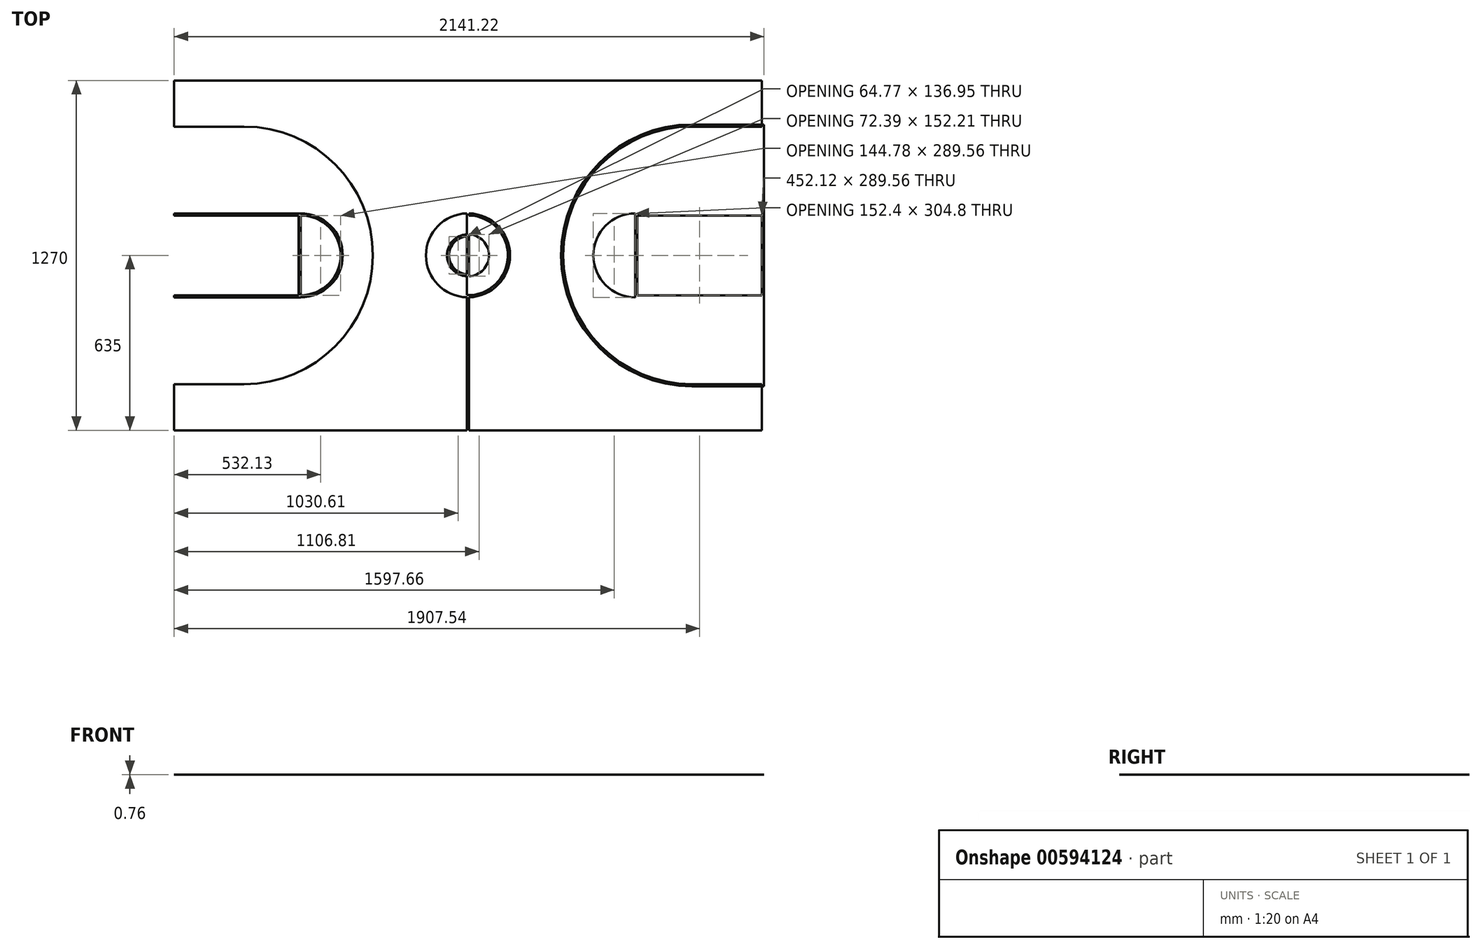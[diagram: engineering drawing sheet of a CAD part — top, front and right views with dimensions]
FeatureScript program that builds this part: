
annotation { "Feature Type Name" : "Feature", "Feature Type Description" : "" }
export const myFeature = defineFeature(function(context is Context, id is Id, definition is map)
    precondition{}
    {
        {
            var Q0;
            Q0=qCreatedBy(makeId("Top.planeOp"),FACE);
            var sketch = newSketch(context, id + "F0", { "sketchPlane" : qUnion([Q0])});
            skLineSegment(sketch, "E0.bottom", {"start": v(-1066.8, -635) * mm, "end": v(1066.8, -635) * mm});
            skLineSegment(sketch, "E0.top", {"start": v(-1066.8, 635) * mm, "end": v(1066.8, 635) * mm});
            skLineSegment(sketch, "E0.left", {"start": v(-1066.8, -635) * mm, "end": v(-1066.8, 635) * mm});
            skLineSegment(sketch, "E0.right", {"start": v(1066.8, -635) * mm, "end": v(1066.8, 635) * mm});
            skPoint(sketch, "E0.middle", {"position": v(0, 0) * mm});
            skLineSegment(sketch, "E1.bottom", {"start": v(-3.81, -635) * mm, "end": v(3.81, -635) * mm});
            skLineSegment(sketch, "E1.top", {"start": v(-3.81, 635) * mm, "end": v(3.81, 635) * mm});
            skLineSegment(sketch, "E1.left", {"start": v(-3.81, -635) * mm, "end": v(-3.81, 635) * mm});
            skLineSegment(sketch, "E1.right", {"start": v(3.81, -635) * mm, "end": v(3.81, 635) * mm});
            skCircle(sketch, "E2", {"center": v(0, 0) * mm, "radius": 152.4 * mm});
            skCircle(sketch, "E3", {"center": v(0, 0) * mm, "radius": 144.78 * mm});
            skCircle(sketch, "E4", {"center": v(0, 0) * mm, "radius": 76.2 * mm});
            skCircle(sketch, "E5", {"center": v(0, 0) * mm, "radius": 68.58 * mm});
            skPoint(sketch, "E6.endSnap0", {"position": v(-1066.8, 0) * mm});
            skLineSegment(sketch, "E7.bottom", {"start": v(-1066.8, -152.4) * mm, "end": v(-607.06, -152.4) * mm});
            skLineSegment(sketch, "E7.top", {"start": v(-1066.8, 152.4) * mm, "end": v(-607.06, 152.4) * mm});
            skLineSegment(sketch, "E7.left", {"start": v(-1066.8, -152.4) * mm, "end": v(-1066.8, 152.4) * mm});
            skLineSegment(sketch, "E7.right", {"start": v(-607.06, -152.4) * mm, "end": v(-607.06, 152.4) * mm});
            skPoint(sketch, "E7.middle", {"position": v(-836.93, 0) * mm});
            skPoint(sketch, "E6.end.orphan", {"position": v(-607.06, 0) * mm});
            skArc(sketch, "E8", {"start": v(-607.06, -152.4) * mm, "mid": v(-454.66, 0) * mm, "end": v(-607.06, 152.4) * mm});
            skLineSegment(sketch, "E9", {"start": v(-1066.8, 635) * mm, "end": v(-1066.8, 474.98) * mm});
            skLineSegment(sketch, "E10", {"start": v(-1066.8, -635) * mm, "end": v(-1066.8, -474.98) * mm});
            skLineSegment(sketch, "E11", {"start": v(-1066.8, 474.98) * mm, "end": v(-812.8, 474.98) * mm});
            skLineSegment(sketch, "E12", {"start": v(-1066.8, -474.98) * mm, "end": v(-812.8, -474.98) * mm});
            skArc(sketch, "E13", {"start": v(-812.8, -474.98) * mm, "mid": v(-337.82, 0) * mm, "end": v(-812.8, 474.98) * mm});
            skLineSegment(sketch, "E14", {"start": v(0, 635) * mm, "end": v(0, -635) * mm});
            skArc(sketch, "E15.MirrorCS", {"start": v(812.8, -474.98) * mm, "mid": v(337.82, 0) * mm, "end": v(812.8, 474.98) * mm});
            skArc(sketch, "E16.MirrorCS", {"start": v(607.06, -152.4) * mm, "mid": v(454.66, 0) * mm, "end": v(607.06, 152.4) * mm});
            skLineSegment(sketch, "E17.MirrorCS", {"start": v(607.06, -152.4) * mm, "end": v(607.06, 152.4) * mm});
            skLineSegment(sketch, "E18.MirrorCS", {"start": v(1066.8, -474.98) * mm, "end": v(812.8, -474.98) * mm});
            skLineSegment(sketch, "E19.MirrorCS", {"start": v(1066.8, 474.98) * mm, "end": v(812.8, 474.98) * mm});
            skLineSegment(sketch, "E20.MirrorCS", {"start": v(1066.8, 152.4) * mm, "end": v(607.06, 152.4) * mm});
            skLineSegment(sketch, "E21.MirrorCS", {"start": v(1066.8, -152.4) * mm, "end": v(607.06, -152.4) * mm});
            skLineSegment(sketch, "E22", {"start": v(-1066.8, 474.98) * mm, "end": v(-1066.8, 467.36) * mm});
            skLineSegment(sketch, "E23", {"start": v(-1066.8, 467.36) * mm, "end": v(-812.8, 467.36) * mm});
            skLineSegment(sketch, "E24", {"start": v(-812.8, 467.36) * mm, "end": v(-812.8, 474.98) * mm});
            skLineSegment(sketch, "E25", {"start": v(-1066.8, -474.98) * mm, "end": v(-1066.8, -467.36) * mm});
            skLineSegment(sketch, "E26", {"start": v(-1066.8, -467.36) * mm, "end": v(-812.8, -467.36) * mm});
            skArc(sketch, "E27", {"start": v(-812.8, -467.36) * mm, "mid": v(-345.44, 0) * mm, "end": v(-812.8, 467.36) * mm});
            skLineSegment(sketch, "E28", {"start": v(-1066.8, 152.4) * mm, "end": v(-1066.8, 144.78) * mm});
            skLineSegment(sketch, "E29", {"start": v(-1066.8, 144.78) * mm, "end": v(-607.06, 144.78) * mm});
            skLineSegment(sketch, "E30", {"start": v(-1066.8, -152.4) * mm, "end": v(-1066.8, -144.78) * mm});
            skLineSegment(sketch, "E31", {"start": v(-1066.8, -144.78) * mm, "end": v(-607.06, -144.78) * mm});
            skLineSegment(sketch, "E32", {"start": v(-607.06, 152.4) * mm, "end": v(-614.68, 152.4) * mm});
            skLineSegment(sketch, "E33", {"start": v(-614.68, 152.4) * mm, "end": v(-614.68, -152.4) * mm});
            skLineSegment(sketch, "E34", {"start": v(-614.68, -152.4) * mm, "end": v(-607.06, -152.4) * mm});
            skArc(sketch, "E35", {"start": v(-607.06, -144.78) * mm, "mid": v(-462.28, 0) * mm, "end": v(-607.06, 144.78) * mm});
            skArc(sketch, "E36.MirrorCS", {"start": v(812.8, -467.36) * mm, "mid": v(345.44, 0) * mm, "end": v(812.8, 467.36) * mm});
            skArc(sketch, "E37.MirrorCS", {"start": v(607.06, -144.78) * mm, "mid": v(462.28, 0) * mm, "end": v(607.06, 144.78) * mm});
            skLineSegment(sketch, "E38.MirrorCS", {"start": v(614.68, 152.4) * mm, "end": v(614.68, -152.4) * mm});
            skLineSegment(sketch, "E39.MirrorCS", {"start": v(1066.8, -144.78) * mm, "end": v(607.06, -144.78) * mm});
            skLineSegment(sketch, "E40.MirrorCS", {"start": v(1066.8, 144.78) * mm, "end": v(607.06, 144.78) * mm});
            skLineSegment(sketch, "E41.MirrorCS", {"start": v(1066.8, -467.36) * mm, "end": v(812.8, -467.36) * mm});
            skLineSegment(sketch, "E42.MirrorCS", {"start": v(1066.8, 467.36) * mm, "end": v(812.8, 467.36) * mm});
            skLineSegment(sketch, "E43", {"start": v(1066.8, 474.98) * mm, "end": v(1074.42, 474.98) * mm});
            skLineSegment(sketch, "E44", {"start": v(1074.42, 474.98) * mm, "end": v(1074.42, -474.98) * mm});
            skLineSegment(sketch, "E45", {"start": v(1074.42, -474.98) * mm, "end": v(1066.8, -474.98) * mm});
            skLineSegment(sketch, "E46.MirrorCS", {"start": v(-1074.42, -474.98) * mm, "end": v(-1066.8, -474.98) * mm});
            skLineSegment(sketch, "E47.MirrorCS", {"start": v(-1074.42, 474.98) * mm, "end": v(-1074.42, -474.98) * mm});
            skLineSegment(sketch, "E48.MirrorCS", {"start": v(-1066.8, 474.98) * mm, "end": v(-1074.42, 474.98) * mm});
            skSolve(sketch);
        }
        {
            var Q0;
            Q0=makeQuery(id+"F0.imprint","IMPRINT",FACE,{"disambiguationData":[TD([[makeQuery(id+"F0.imprint","IMPRINT",EDGE,{"derivedFrom":sQuery(id+"F0.wireOp",EDGE,"E12")}),1.0]])]});
            var Q1;
            Q1=makeQuery(id+"F0.imprint","IMPRINT",FACE,{"disambiguationData":[TD([[makeQuery(id+"F0.imprint","IMPRINT",EDGE,{"derivedFrom":sQuery(id+"F0.wireOp",EDGE,"E11")}),-1.0]])]});
            var Q2;
            {var subQ1=sQuery(id+"F0.wireOp",EDGE,"E29");var subQ6=sQuery(id+"F0.wireOp",EDGE,"E33");var subQ7=makeQuery(id+"F0.imprint","INTERSECT",VERTEX,{"derivedFrom":[subQ1,subQ6]});Q2=makeQuery(id+"F0.imprint","IMPRINT",FACE,{"disambiguationData":[TD([[makeQuery(id+"F0.imprint","IMPRINT",EDGE,{"disambiguationData":[TD([[subQ7,-1.0]])],"derivedFrom":subQ6}),1.0]])]});}
            var Q3;
            {var subQ0=sQuery(id+"F0.wireOp",EDGE,"E7.top");Q3=makeQuery(id+"F0.imprint","IMPRINT",FACE,{"disambiguationData":[TD([[makeQuery(id+"F0.imprint","IMPRINT",EDGE,{"derivedFrom":subQ0}),-1.0]])]});}
            var Q4;
            {var subQ0=sQuery(id+"F0.wireOp",EDGE,"E32");Q4=makeQuery(id+"F0.imprint","IMPRINT",FACE,{"disambiguationData":[TD([[makeQuery(id+"F0.imprint","IMPRINT",EDGE,{"derivedFrom":subQ0}),1.0]])]});}
            var Q5;
            {var subQ0=sQuery(id+"F0.wireOp",EDGE,"E8");Q5=makeQuery(id+"F0.imprint","IMPRINT",FACE,{"disambiguationData":[TD([[makeQuery(id+"F0.imprint","IMPRINT",EDGE,{"derivedFrom":subQ0}),1.0]])]});}
            var Q6;
            {var subQ0=sQuery(id+"F0.wireOp",EDGE,"E7.bottom");Q6=makeQuery(id+"F0.imprint","IMPRINT",FACE,{"disambiguationData":[TD([[makeQuery(id+"F0.imprint","IMPRINT",EDGE,{"derivedFrom":subQ0}),1.0]])]});}
            var Q7;
            {var subQ0=sQuery(id+"F0.wireOp",EDGE,"E34");Q7=makeQuery(id+"F0.imprint","IMPRINT",FACE,{"disambiguationData":[TD([[makeQuery(id+"F0.imprint","IMPRINT",EDGE,{"derivedFrom":subQ0}),1.0]])]});}
            var Q8;
            {var subQ0=sQuery(id+"F0.wireOp",EDGE,"E4");var subQ1=sQuery(id+"F0.wireOp",EDGE,"E1.left");var subQ2=makeQuery(id+"F0.imprint","INTERSECT",VERTEX,{"disambiguationData":[OD(0.0)],"derivedFrom":[subQ1,subQ0]});Q8=makeQuery(id+"F0.imprint","IMPRINT",FACE,{"disambiguationData":[TD([[makeQuery(id+"F0.imprint","IMPRINT",EDGE,{"disambiguationData":[TD([[subQ2,-1.0]])],"derivedFrom":subQ1}),1.0]])]});}
            var Q9;
            {var subQ0=sQuery(id+"F0.wireOp",EDGE,"E4");var subQ1=sQuery(id+"F0.wireOp",EDGE,"E1.right");var subQ2=makeQuery(id+"F0.imprint","INTERSECT",VERTEX,{"disambiguationData":[OD(0.0)],"derivedFrom":[subQ1,subQ0]});Q9=makeQuery(id+"F0.imprint","IMPRINT",FACE,{"disambiguationData":[TD([[makeQuery(id+"F0.imprint","IMPRINT",EDGE,{"disambiguationData":[TD([[subQ2,-1.0]])],"derivedFrom":subQ1}),-1.0]])]});}
            var Q10;
            {var subQ0=sQuery(id+"F0.wireOp",EDGE,"E5");var subQ1=sQuery(id+"F0.wireOp",EDGE,"E1.right");var subQ2=makeQuery(id+"F0.imprint","INTERSECT",VERTEX,{"disambiguationData":[OD(1.0)],"derivedFrom":[subQ1,subQ0]});Q10=makeQuery(id+"F0.imprint","IMPRINT",FACE,{"disambiguationData":[TD([[makeQuery(id+"F0.imprint","IMPRINT",EDGE,{"disambiguationData":[TD([[subQ2,-1.0]])],"derivedFrom":subQ1}),1.0]])]});}
            var Q11;
            {var subQ0=sQuery(id+"F0.wireOp",EDGE,"E5");var subQ1=sQuery(id+"F0.wireOp",EDGE,"E1.left");var subQ2=makeQuery(id+"F0.imprint","INTERSECT",VERTEX,{"disambiguationData":[OD(1.0)],"derivedFrom":[subQ1,subQ0]});Q11=makeQuery(id+"F0.imprint","IMPRINT",FACE,{"disambiguationData":[TD([[makeQuery(id+"F0.imprint","IMPRINT",EDGE,{"disambiguationData":[TD([[subQ2,-1.0]])],"derivedFrom":subQ1}),-1.0]])]});}
            var Q12;
            {var subQ0=sQuery(id+"F0.wireOp",EDGE,"E2");var subQ1=sQuery(id+"F0.wireOp",EDGE,"E1.left");var subQ2=makeQuery(id+"F0.imprint","INTERSECT",VERTEX,{"disambiguationData":[OD(0.0)],"derivedFrom":[subQ1,subQ0]});Q12=makeQuery(id+"F0.imprint","IMPRINT",FACE,{"disambiguationData":[TD([[makeQuery(id+"F0.imprint","IMPRINT",EDGE,{"disambiguationData":[TD([[subQ2,-1.0]])],"derivedFrom":subQ1}),1.0]])]});}
            var Q13;
            {var subQ0=sQuery(id+"F0.wireOp",EDGE,"E3");var subQ1=sQuery(id+"F0.wireOp",EDGE,"E1.left");var subQ2=makeQuery(id+"F0.imprint","INTERSECT",VERTEX,{"disambiguationData":[OD(1.0)],"derivedFrom":[subQ1,subQ0]});Q13=makeQuery(id+"F0.imprint","IMPRINT",FACE,{"disambiguationData":[TD([[makeQuery(id+"F0.imprint","IMPRINT",EDGE,{"disambiguationData":[TD([[subQ2,-1.0]])],"derivedFrom":subQ1}),-1.0]])]});}
            var Q14;
            {var subQ0=sQuery(id+"F0.wireOp",EDGE,"E3");var subQ1=sQuery(id+"F0.wireOp",EDGE,"E1.right");var subQ2=makeQuery(id+"F0.imprint","INTERSECT",VERTEX,{"disambiguationData":[OD(1.0)],"derivedFrom":[subQ1,subQ0]});Q14=makeQuery(id+"F0.imprint","IMPRINT",FACE,{"disambiguationData":[TD([[makeQuery(id+"F0.imprint","IMPRINT",EDGE,{"disambiguationData":[TD([[subQ2,-1.0]])],"derivedFrom":subQ1}),1.0]])]});}
            var Q15;
            {var subQ0=sQuery(id+"F0.wireOp",EDGE,"E2");var subQ1=sQuery(id+"F0.wireOp",EDGE,"E1.right");var subQ2=makeQuery(id+"F0.imprint","INTERSECT",VERTEX,{"disambiguationData":[OD(0.0)],"derivedFrom":[subQ1,subQ0]});Q15=makeQuery(id+"F0.imprint","IMPRINT",FACE,{"disambiguationData":[TD([[makeQuery(id+"F0.imprint","IMPRINT",EDGE,{"disambiguationData":[TD([[subQ2,-1.0]])],"derivedFrom":subQ1}),-1.0]])]});}
            var Q16;
            {var subQ0=sQuery(id+"F0.wireOp",EDGE,"E4");var subQ1=sQuery(id+"F0.wireOp",EDGE,"E1.left");var subQ2=makeQuery(id+"F0.imprint","INTERSECT",VERTEX,{"disambiguationData":[OD(0.0)],"derivedFrom":[subQ1,subQ0]});Q16=makeQuery(id+"F0.imprint","IMPRINT",FACE,{"disambiguationData":[TD([[makeQuery(id+"F0.imprint","IMPRINT",EDGE,{"disambiguationData":[TD([[subQ2,-1.0]])],"derivedFrom":subQ1}),-1.0]])]});}
            var Q17;
            {var subQ0=sQuery(id+"F0.wireOp",EDGE,"E4");var subQ1=sQuery(id+"F0.wireOp",EDGE,"E1.right");var subQ2=makeQuery(id+"F0.imprint","INTERSECT",VERTEX,{"disambiguationData":[OD(0.0)],"derivedFrom":[subQ1,subQ0]});Q17=makeQuery(id+"F0.imprint","IMPRINT",FACE,{"disambiguationData":[TD([[makeQuery(id+"F0.imprint","IMPRINT",EDGE,{"disambiguationData":[TD([[subQ2,-1.0]])],"derivedFrom":subQ1}),1.0]])]});}
            var Q18;
            {var subQ0=sQuery(id+"F0.wireOp",EDGE,"E2");var subQ1=sQuery(id+"F0.wireOp",EDGE,"E1.left");var subQ2=makeQuery(id+"F0.imprint","INTERSECT",VERTEX,{"disambiguationData":[OD(0.0)],"derivedFrom":[subQ1,subQ0]});Q18=makeQuery(id+"F0.imprint","IMPRINT",FACE,{"disambiguationData":[TD([[makeQuery(id+"F0.imprint","IMPRINT",EDGE,{"disambiguationData":[TD([[subQ2,-1.0]])],"derivedFrom":subQ1}),-1.0]])]});}
            var Q19;
            {var subQ0=sQuery(id+"F0.wireOp",EDGE,"E2");var subQ1=sQuery(id+"F0.wireOp",EDGE,"E1.right");var subQ2=makeQuery(id+"F0.imprint","INTERSECT",VERTEX,{"disambiguationData":[OD(0.0)],"derivedFrom":[subQ1,subQ0]});Q19=makeQuery(id+"F0.imprint","IMPRINT",FACE,{"disambiguationData":[TD([[makeQuery(id+"F0.imprint","IMPRINT",EDGE,{"disambiguationData":[TD([[subQ2,-1.0]])],"derivedFrom":subQ1}),1.0]])]});}
            var Q20;
            Q20=makeQuery(id+"F0.imprint","IMPRINT",FACE,{"disambiguationData":[TD([[makeQuery(id+"F0.imprint","IMPRINT",EDGE,{"derivedFrom":sQuery(id+"F0.wireOp",EDGE,"E15.MirrorCS")}),-1.0]])]});
            var Q21;
            {var subQ0=sQuery(id+"F0.wireOp",EDGE,"E20.MirrorCS");var subQ1=sQuery(id+"F0.wireOp",EDGE,"E0.right");var subQ2=makeQuery(id+"F0.imprint","INTERSECT",VERTEX,{"derivedFrom":[subQ1,subQ0]});Q21=makeQuery(id+"F0.imprint","IMPRINT",FACE,{"disambiguationData":[TD([[makeQuery(id+"F0.imprint","IMPRINT",EDGE,{"disambiguationData":[TD([[subQ2,1.0]])],"derivedFrom":subQ1}),1.0]])]});}
            var Q22;
            {var subQ0=sQuery(id+"F0.wireOp",EDGE,"E20.MirrorCS");var subQ5=sQuery(id+"F0.wireOp",EDGE,"E38.MirrorCS");var subQ6=makeQuery(id+"F0.imprint","INTERSECT",VERTEX,{"derivedFrom":[subQ0,subQ5]});Q22=makeQuery(id+"F0.imprint","IMPRINT",FACE,{"disambiguationData":[TD([[makeQuery(id+"F0.imprint","IMPRINT",EDGE,{"disambiguationData":[TD([[subQ6,-1.0]])],"derivedFrom":subQ5}),-1.0]])]});}
            var Q23;
            {var subQ4=sQuery(id+"F0.wireOp",EDGE,"E40.MirrorCS");var subQ6=sQuery(id+"F0.wireOp",EDGE,"E38.MirrorCS");var subQ7=makeQuery(id+"F0.imprint","INTERSECT",VERTEX,{"derivedFrom":[subQ6,subQ4]});Q23=makeQuery(id+"F0.imprint","IMPRINT",FACE,{"disambiguationData":[TD([[makeQuery(id+"F0.imprint","IMPRINT",EDGE,{"disambiguationData":[TD([[subQ7,-1.0]])],"derivedFrom":subQ6}),-1.0]])]});}
            var Q24;
            {var subQ0=sQuery(id+"F0.wireOp",EDGE,"E16.MirrorCS");Q24=makeQuery(id+"F0.imprint","IMPRINT",FACE,{"disambiguationData":[TD([[makeQuery(id+"F0.imprint","IMPRINT",EDGE,{"derivedFrom":subQ0}),-1.0]])]});}
            var Q25;
            {var subQ0=sQuery(id+"F0.wireOp",EDGE,"E21.MirrorCS");var subQ1=sQuery(id+"F0.wireOp",EDGE,"E0.right");var subQ2=makeQuery(id+"F0.imprint","INTERSECT",VERTEX,{"derivedFrom":[subQ1,subQ0]});Q25=makeQuery(id+"F0.imprint","IMPRINT",FACE,{"disambiguationData":[TD([[makeQuery(id+"F0.imprint","IMPRINT",EDGE,{"disambiguationData":[TD([[subQ2,-1.0]])],"derivedFrom":subQ1}),1.0]])]});}
            var Q26;
            {var subQ0=sQuery(id+"F0.wireOp",EDGE,"E21.MirrorCS");var subQ5=sQuery(id+"F0.wireOp",EDGE,"E38.MirrorCS");var subQ6=makeQuery(id+"F0.imprint","INTERSECT",VERTEX,{"derivedFrom":[subQ0,subQ5]});Q26=makeQuery(id+"F0.imprint","IMPRINT",FACE,{"disambiguationData":[TD([[makeQuery(id+"F0.imprint","IMPRINT",EDGE,{"disambiguationData":[TD([[subQ6,1.0]])],"derivedFrom":subQ5}),-1.0]])]});}
            var Q27;
            {var subQ8=sQuery(id+"F0.wireOp",EDGE,"E43");Q27=makeQuery(id+"F0.imprint","IMPRINT",FACE,{"disambiguationData":[TD([[makeQuery(id+"F0.imprint","IMPRINT",EDGE,{"derivedFrom":subQ8}),-1.0]])]});}
            var Q28;
            Q28=makeQuery(id+"F0.imprint","IMPRINT",FACE,{"disambiguationData":[TD([[makeQuery(id+"F0.imprint","IMPRINT",EDGE,{"derivedFrom":sQuery(id+"F0.wireOp",EDGE,"E7.left")}),1.0]])]});
            var Q29;
            {var subQ0=sQuery(id+"F0.wireOp",EDGE,"E1.left");var subQ5=sQuery(id+"F0.wireOp",EDGE,"E2");var subQ6=makeQuery(id+"F0.imprint","INTERSECT",VERTEX,{"disambiguationData":[OD(1.0)],"derivedFrom":[subQ0,subQ5]});Q29=makeQuery(id+"F0.imprint","IMPRINT",FACE,{"disambiguationData":[TD([[makeQuery(id+"F0.imprint","IMPRINT",EDGE,{"disambiguationData":[TD([[subQ6,1.0]])],"derivedFrom":subQ5}),-1.0]])]});}
            var Q30;
            {var subQ0=sQuery(id+"F0.wireOp",EDGE,"E1.right");var subQ5=sQuery(id+"F0.wireOp",EDGE,"E2");var subQ7=makeQuery(id+"F0.imprint","INTERSECT",VERTEX,{"disambiguationData":[OD(1.0)],"derivedFrom":[subQ0,subQ5]});Q30=makeQuery(id+"F0.imprint","IMPRINT",FACE,{"disambiguationData":[TD([[makeQuery(id+"F0.imprint","IMPRINT",EDGE,{"disambiguationData":[TD([[subQ7,-1.0]])],"derivedFrom":subQ5}),-1.0]])]});}
            var Q31;
            {var subQ0=sQuery(id+"F0.wireOp",EDGE,"E4");var subQ1=sQuery(id+"F0.wireOp",EDGE,"E1.left");var subQ2=makeQuery(id+"F0.imprint","INTERSECT",VERTEX,{"disambiguationData":[OD(1.0)],"derivedFrom":[subQ1,subQ0]});Q31=makeQuery(id+"F0.imprint","IMPRINT",FACE,{"disambiguationData":[TD([[makeQuery(id+"F0.imprint","IMPRINT",EDGE,{"disambiguationData":[TD([[subQ2,-1.0]])],"derivedFrom":subQ1}),-1.0]])]});}
            var Q32;
            {var subQ0=sQuery(id+"F0.wireOp",EDGE,"E4");var subQ1=sQuery(id+"F0.wireOp",EDGE,"E1.right");var subQ2=makeQuery(id+"F0.imprint","INTERSECT",VERTEX,{"disambiguationData":[OD(1.0)],"derivedFrom":[subQ1,subQ0]});Q32=makeQuery(id+"F0.imprint","IMPRINT",FACE,{"disambiguationData":[TD([[makeQuery(id+"F0.imprint","IMPRINT",EDGE,{"disambiguationData":[TD([[subQ2,-1.0]])],"derivedFrom":subQ1}),1.0]])]});}
            var Q33;
            {var subQ0=sQuery(id+"F0.wireOp",EDGE,"E5");var subQ1=sQuery(id+"F0.wireOp",EDGE,"E1.left");var subQ2=makeQuery(id+"F0.imprint","INTERSECT",VERTEX,{"disambiguationData":[OD(0.0)],"derivedFrom":[subQ1,subQ0]});Q33=makeQuery(id+"F0.imprint","IMPRINT",FACE,{"disambiguationData":[TD([[makeQuery(id+"F0.imprint","IMPRINT",EDGE,{"disambiguationData":[TD([[subQ2,-1.0]])],"derivedFrom":subQ1}),-1.0]])]});}
            var Q34;
            {var subQ0=sQuery(id+"F0.wireOp",EDGE,"E5");var subQ1=sQuery(id+"F0.wireOp",EDGE,"E1.right");var subQ2=makeQuery(id+"F0.imprint","INTERSECT",VERTEX,{"disambiguationData":[OD(0.0)],"derivedFrom":[subQ1,subQ0]});Q34=makeQuery(id+"F0.imprint","IMPRINT",FACE,{"disambiguationData":[TD([[makeQuery(id+"F0.imprint","IMPRINT",EDGE,{"disambiguationData":[TD([[subQ2,-1.0]])],"derivedFrom":subQ1}),1.0]])]});}
            var Q35;
            {var subQ0=sQuery(id+"F0.wireOp",EDGE,"E3");var subQ1=sQuery(id+"F0.wireOp",EDGE,"E1.left");var subQ2=makeQuery(id+"F0.imprint","INTERSECT",VERTEX,{"disambiguationData":[OD(0.0)],"derivedFrom":[subQ1,subQ0]});Q35=makeQuery(id+"F0.imprint","IMPRINT",FACE,{"disambiguationData":[TD([[makeQuery(id+"F0.imprint","IMPRINT",EDGE,{"disambiguationData":[TD([[subQ2,-1.0]])],"derivedFrom":subQ1}),-1.0]])]});}
            var Q36;
            {var subQ0=sQuery(id+"F0.wireOp",EDGE,"E3");var subQ1=sQuery(id+"F0.wireOp",EDGE,"E1.right");var subQ2=makeQuery(id+"F0.imprint","INTERSECT",VERTEX,{"disambiguationData":[OD(0.0)],"derivedFrom":[subQ1,subQ0]});Q36=makeQuery(id+"F0.imprint","IMPRINT",FACE,{"disambiguationData":[TD([[makeQuery(id+"F0.imprint","IMPRINT",EDGE,{"disambiguationData":[TD([[subQ2,-1.0]])],"derivedFrom":subQ1}),1.0]])]});}
            var Q37;
            {var subQ0=sQuery(id+"F0.wireOp",EDGE,"E1.left");var subQ5=sQuery(id+"F0.wireOp",EDGE,"E2");var subQ6=makeQuery(id+"F0.imprint","INTERSECT",VERTEX,{"disambiguationData":[OD(0.0)],"derivedFrom":[subQ0,subQ5]});Q37=makeQuery(id+"F0.imprint","IMPRINT",FACE,{"disambiguationData":[TD([[makeQuery(id+"F0.imprint","IMPRINT",EDGE,{"disambiguationData":[TD([[subQ6,-1.0]])],"derivedFrom":subQ5}),-1.0]])]});}
            var Q38;
            {var subQ0=sQuery(id+"F0.wireOp",EDGE,"E1.right");var subQ5=sQuery(id+"F0.wireOp",EDGE,"E2");var subQ6=makeQuery(id+"F0.imprint","INTERSECT",VERTEX,{"disambiguationData":[OD(0.0)],"derivedFrom":[subQ0,subQ5]});Q38=makeQuery(id+"F0.imprint","IMPRINT",FACE,{"disambiguationData":[TD([[makeQuery(id+"F0.imprint","IMPRINT",EDGE,{"disambiguationData":[TD([[subQ6,1.0]])],"derivedFrom":subQ5}),-1.0]])]});}
            extrude(context, id + "F1", {"entities" : qUnion([Q0, Q1, Q2, Q3, Q4, Q5, Q6, Q7, Q8, Q9, Q10, Q11, Q12, Q13, Q14, Q15, Q16, Q17, Q18, Q19, Q20, Q21, Q22, Q23, Q24, Q25, Q26, Q27, Q28, Q29, Q30, Q31, Q32, Q33, Q34, Q35, Q36, Q37, Q38]), "depth" : 0.76 * mm, "offsetDistance" : 25.4 * mm});
        }
    });
